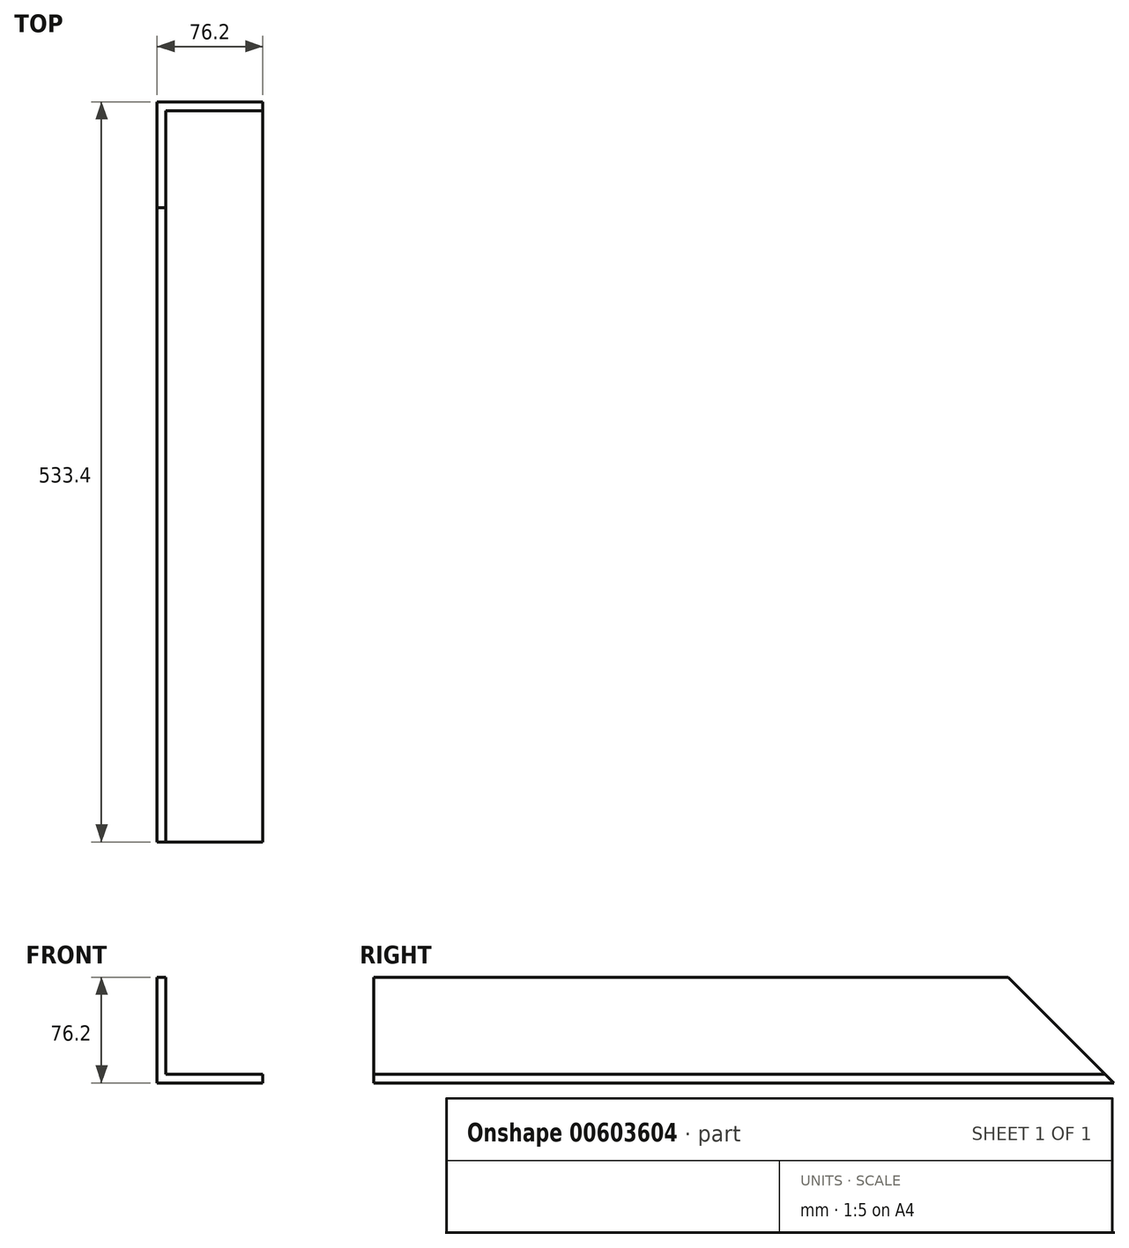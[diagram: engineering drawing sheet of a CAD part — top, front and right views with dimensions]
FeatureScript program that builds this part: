
annotation { "Feature Type Name" : "Feature", "Feature Type Description" : "" }
export const myFeature = defineFeature(function(context is Context, id is Id, definition is map)
    precondition{}
    {
        {
            var Q0;
            Q0=qCreatedBy(makeId("Front.planeOp"),FACE);
            var sketch = newSketch(context, id + "F0", { "sketchPlane" : qUnion([Q0])});
            skLineSegment(sketch, "E0.bottom", {"start": v(38.1, -38.1) * mm, "end": v(-38.1, -38.1) * mm});
            skLineSegment(sketch, "E0.top", {"start": v(-31.75, 38.1) * mm, "end": v(-38.1, 38.1) * mm});
            skLineSegment(sketch, "E0.left", {"start": v(38.1, -38.1) * mm, "end": v(38.1, -31.75) * mm});
            skLineSegment(sketch, "E0.right", {"start": v(-38.1, -38.1) * mm, "end": v(-38.1, 38.1) * mm});
            skPoint(sketch, "E0.middle", {"position": v(0, 0) * mm});
            skLineSegment(sketch, "E1.0", {"start": v(-31.75, -31.75) * mm, "end": v(-31.75, 38.1) * mm});
            skLineSegment(sketch, "E2.0", {"start": v(38.1, -31.75) * mm, "end": v(-31.75, -31.75) * mm});
            skPoint(sketch, "E3.orphan", {"position": v(38.1, 38.1) * mm});
            skSolve(sketch);
        }
        {
            var Q0;
            Q0 = qSketchRegion(id + "F0", true);
            extrude(context, id + "F1", {"entities" : qUnion([Q0]), "endBound" : BoundingType.SYMMETRIC, "depth" : 533.4 * mm, "offsetDistance" : 25.4 * mm});
        }
        {
            var Q0;
            Q0=makeQuery(id+"F1.opExtrude","SWEPT_FACE",FACE,{"disambiguationData":[OSD([sQuery(id+"F0.wireOp",EDGE,"E0.right")])]});
            var sketch = newSketch(context, id + "F2", { "sketchPlane" : qUnion([Q0])});
            skLineSegment(sketch, "E4", {"start": v(-266.7, -38.1) * mm, "end": v(-190.5, 38.1) * mm});
            skLineSegment(sketch, "E5", {"start": v(-190.5, 38.1) * mm, "end": v(-266.7, 38.1) * mm});
            skLineSegment(sketch, "E6", {"start": v(-266.7, 38.1) * mm, "end": v(-266.7, -38.1) * mm});
            skSolve(sketch);
        }
        {
            var Q0;
            Q0 = qSketchRegion(id + "F2", true);
            extrude(context, id + "F3", {"entities" : qUnion([Q0]), "operationType" : NewBodyOperationType.REMOVE, "oppositeDirection" : true, "depth" : 76.2 * mm, "offsetDistance" : 25.4 * mm});
        }
    });
